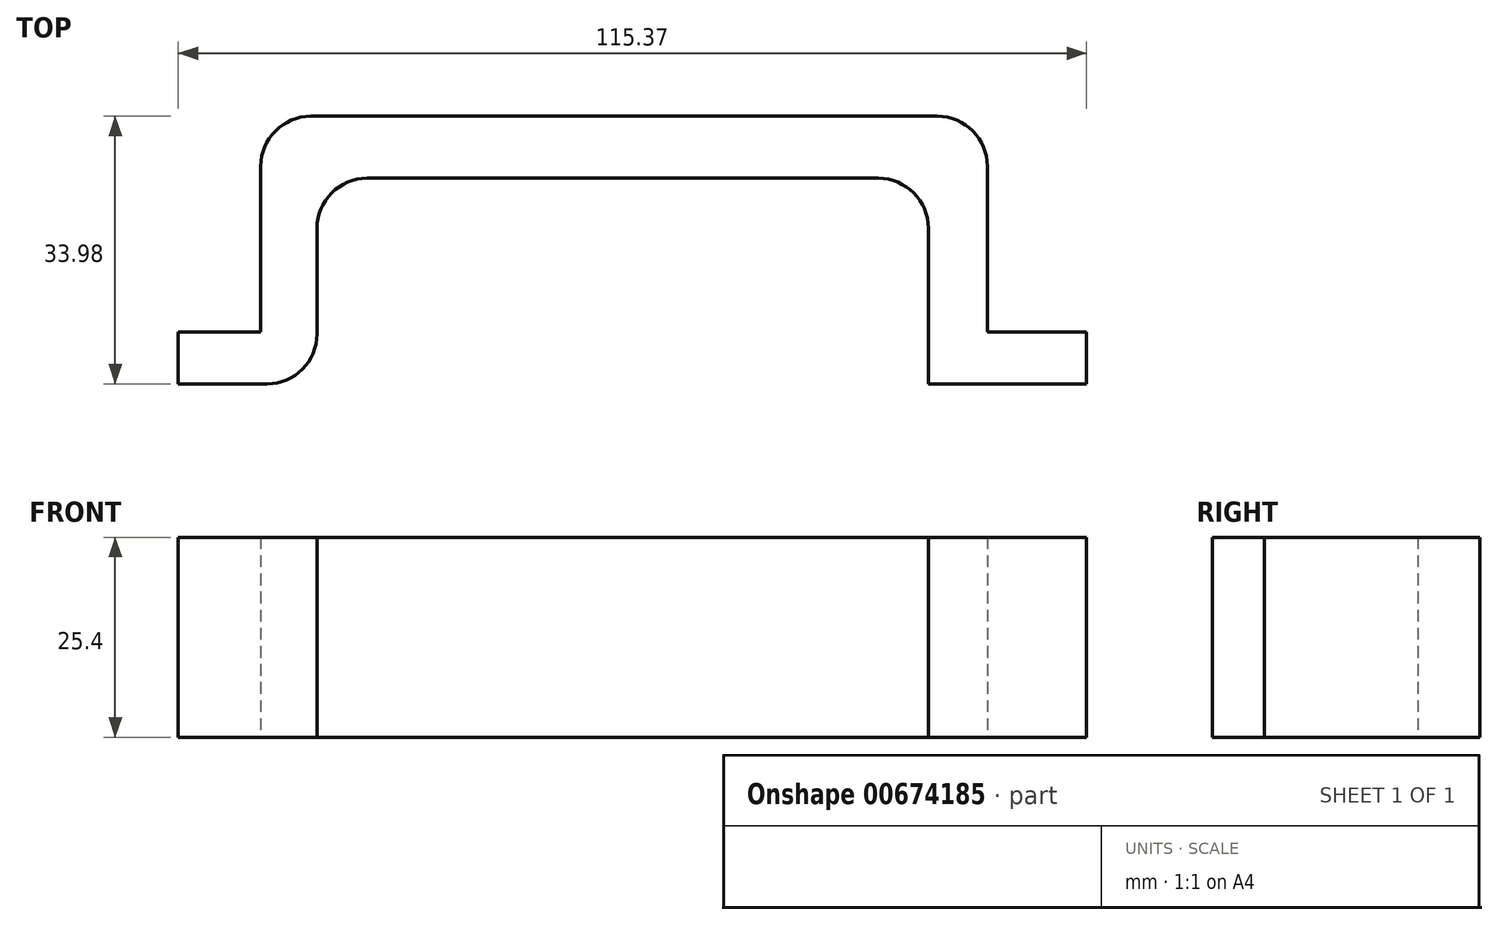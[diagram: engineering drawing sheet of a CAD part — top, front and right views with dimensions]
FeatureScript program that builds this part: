
annotation { "Feature Type Name" : "Feature", "Feature Type Description" : "" }
export const myFeature = defineFeature(function(context is Context, id is Id, definition is map)
    precondition{}
    {
        {
            var Q0;
            Q0=qCreatedBy(makeId("Top.planeOp"),FACE);
            var sketch = newSketch(context, id + "F0", { "sketchPlane" : qUnion([Q0])});
            skLineSegment(sketch, "E0", {"start": v(-63.15, -15.41) * mm, "end": v(-51.87, -15.41) * mm});
            skLineSegment(sketch, "E1", {"start": v(-45.52, -9.06) * mm, "end": v(-45.52, 4.34) * mm});
            skLineSegment(sketch, "E2", {"start": v(-39.17, 10.7) * mm, "end": v(25.78, 10.7) * mm});
            skLineSegment(sketch, "E3", {"start": v(32.13, 4.34) * mm, "end": v(32.13, -15.41) * mm});
            skLineSegment(sketch, "E4", {"start": v(32.13, -15.41) * mm, "end": v(52.22, -15.41) * mm});
            skLineSegment(sketch, "E5", {"start": v(52.22, -15.41) * mm, "end": v(52.22, -8.82) * mm});
            skLineSegment(sketch, "E6", {"start": v(52.22, -8.82) * mm, "end": v(39.63, -8.82) * mm});
            skLineSegment(sketch, "E7", {"start": v(39.63, -8.82) * mm, "end": v(39.63, 12.22) * mm});
            skLineSegment(sketch, "E8", {"start": v(33.28, 18.57) * mm, "end": v(-46.31, 18.57) * mm});
            skLineSegment(sketch, "E9", {"start": v(-52.66, 12.22) * mm, "end": v(-52.66, -8.82) * mm});
            skLineSegment(sketch, "E10", {"start": v(-52.66, -8.82) * mm, "end": v(-63.15, -8.82) * mm});
            skLineSegment(sketch, "E11", {"start": v(-63.15, -8.82) * mm, "end": v(-63.15, -15.41) * mm});
            skPoint(sketch, "E12.visualSharp", {"position": v(39.63, 18.57) * mm});
            skArc(sketch, "E12.filletArc", {"start": v(39.63, 12.22) * mm, "mid": v(37.77, 16.7) * mm, "end": v(33.28, 18.57) * mm});
            skPoint(sketch, "E13.visualSharp", {"position": v(32.13, 10.7) * mm});
            skArc(sketch, "E13.filletArc", {"start": v(32.13, 4.34) * mm, "mid": v(30.27, 8.84) * mm, "end": v(25.78, 10.7) * mm});
            skPoint(sketch, "E14.visualSharp", {"position": v(-45.52, 10.7) * mm});
            skArc(sketch, "E14.filletArc", {"start": v(-39.17, 10.7) * mm, "mid": v(-43.66, 8.84) * mm, "end": v(-45.52, 4.34) * mm});
            skPoint(sketch, "E15.visualSharp", {"position": v(-52.66, 18.57) * mm});
            skArc(sketch, "E15.filletArc", {"start": v(-46.31, 18.57) * mm, "mid": v(-50.8, 16.7) * mm, "end": v(-52.66, 12.22) * mm});
            skPoint(sketch, "E16.visualSharp", {"position": v(-45.52, -15.41) * mm});
            skArc(sketch, "E16.filletArc", {"start": v(-51.87, -15.41) * mm, "mid": v(-47.38, -13.55) * mm, "end": v(-45.52, -9.06) * mm});
            skSolve(sketch);
        }
        {
            var Q0;
            Q0=makeQuery(id+"F0.imprint","IMPRINT",FACE,{"disambiguationData":[TD([[makeQuery(id+"F0.imprint","IMPRINT",EDGE,{"derivedFrom":sQuery(id+"F0.wireOp",EDGE,"E0")}),1.0]])]});
            extrude(context, id + "F1", {"entities" : qUnion([Q0]), "depth" : 25.4 * mm, "offsetDistance" : 25.4 * mm});
        }
    });
